# Revit family: 46601
name_source: partatom
category: Generic Models
revit_build: Autodesk Revit 2018 (Build: 20170223_1515(x64)
units: mm (PartAtom-declared; Revit-internal decimal feet)

## family parameters
Can host rebar = No
Cut with Voids When Loaded = No
Host = Face
OmniClass Number = 23.80.70.00
OmniClass Title = Lighting
Part Type = Normal
Room Calculation Point = No
Round Connector Dimension = Use Diameter
Shared = No

## types (1)
- 0046603 EMERGENCY PACK SELF TEST/DALI 50V-200V
    Assembly Code = D5020200
    Cost = 0 $
    Default Elevation = 24 mm  [stored 0.0787402 ft]
    Description = The emergency kit enables conversion of general lighting for emergency operation. It is used for driving luminaires with forward voltages (Vf) of 50V to 200V, and built-in adaptability that allows for optimum output current based on the forward voltage of the specific light engine for a more precise match to the controlled LED scheme. Features: Suitable for independent mounting, Auto load detecting,  Compatible with leading brands of mains drivers,  SmartCharge technology for NiMH batteries, Test-switch function, Battery deep-discharge protection, Compatible with NiMH batteries, 3-hour rated emergency duration,  Supply current (max) 25mA. Ambient temperature (ta): 0°C to +35°C. Max case temperature (tc) +70°C. Conductor size : 0.2 to 1.5mm2. DALI functionality. NiNH battery. Product contains a charging regime that prolongs battery life and reduces parasitic power consumption during the product life cycle. By controlling battery temperature this results in energy saving and reduction in maintenance costs throughout the premises.
    Height = 24 mm  [stored 0.0787402 ft]
    Length = 546 mm  [stored 1.79134 ft]
    Material_1_SYL = <By Category>
    Material_2_SYL = <By Category>
    Material_3_SYL = <By Category>
    Material_4_SYL = <By Category>
    Model = EMERGENCY PACK SELF TEST/DALI MONITORING 50V-200V
    Type Image = <None>
    URL = 0
    Width = 41 mm  [stored 0.134514 ft]

note: [stored X ft] marks values corroborated as IEEE doubles in the binary element streams (Revit-internal decimal feet)

## geometry (parser evidence)
native form markers: Sweep x1
no freeform markers — native parametric forms only
